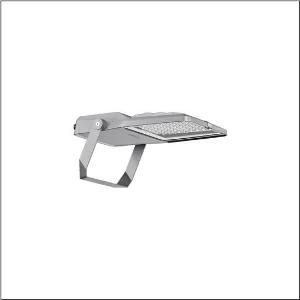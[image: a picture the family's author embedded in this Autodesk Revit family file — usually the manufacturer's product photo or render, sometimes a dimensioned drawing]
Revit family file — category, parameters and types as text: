
# Revit family: floodlight_fl_21_mini___pl61_5xa7776b2c1a_e1cc
name_source: partatom
category: Lighting Fixtures
units: mm (PartAtom-declared; Revit-internal decimal feet)

## family parameters
Cut with Voids When Loaded = No
Host = Face
Light Source = No
Part Type = Normal
Room Calculation Point = No
Round Connector Dimension = Use Diameter
Shared = No

## types (1)
- --- (1 x LED, 6110 lm, 45.7 W, 3000K)
    Apparent Load = 46 VA
    CIE Flux Codes = 33 65 98 100 100
    Color Rendering = 70
    Color Temperature = 3000K
    Default Elevation = 1800 mm
    Description = Floodlight FL 21 mini, floodlight, primary light control with lens, of PMMA, primary optical cover: protective disc, of toughened safety glass, transparent, light distribution: PL61, light emission: direct distribution, installation type: surface-mounted, LED, High Power LED, rated luminous flux: 6.110lm, luminous efficacy: 134lm/W, light colour: 730, colour temperature: 3000K, control: flexible luminous flux parameterisation, time-dependent luminous flux control, constant luminous flux control, overheat protection, presetting dimming logarithmic, with terminal, 6-pole, mains connection: 220..240V, AC, 50/60Hz, start of lifetime: 46W, end of service life: 48W, reduction: 22W, luminaire housing, of diecast aluminium, powder-coated, Siteco® metallic grey (DB 702S), corrosivity category C5 mid according to DIN EN ISO 12944, sealing non-destructively replaceable, mounting bracket, of steel, galvanised, powder-coated, Siteco® metallic grey (DB 702S), Smart Interface below and above, protection rating (complete): IP66, insulation class (complete): insulation class II (safety insulation), certification: CE, ENEC, VDE, protection symbol: D, impact resistance: IK08, permissible operating ambient temperature: -40..+40°C, permissible operating ambient temperature for outdoor applications: -40..+50°C, standard: DIN EN 12944, LABS conformity tested according to VDMA 24364:2018-05, packaging unit: 1 piece

Light Distribution: PL61
    Height = 70 mm
    Lamp = 1 x LED
    Lamp Light Flux = 6110 lm
    Lamp Power = 45.7 W
    Lamp count = 1
    Length = 485 mm
    Luminous efficacy = 134 lm/W
    Manufacturer = Siteco
    ModVariant = No
    Model = 5XA7776B2C1A
    Number of Poles = 1
    OnlyDefault = Yes
    Power Factor = 1
    Product Name = Floodlight FL 21 mini | PL61
    Product group = floodlight | pylon annexe
    ProductGroupID = 6200
    Protection Class = Protection class II
    Protection Degree = IP 66
    RLX_Detail_Level = 1
    RLX_Emergency_Light_Flux = 0 lm
    RLX_Emergency_Type = 0
    RLX_Emergency_Type_DB = No
    RlxData = <blob elided: 95921 chars, md5=8e675ca1>
    Socket = socket
    Standby Power = 0 W
    System Light Flux = 6110 lm
    System Power = 46 W
    Type Comments = factory setting: luminous flux: 100 % | dim-lin: 254 | 463 mA
    Type Image = l_1006845.jpg
    URL = http://relux.com
    VarID = @adj_105235
    Voltage = 0 V
    Weight = 0.00 kg
    Width = 337 mm

## geometry (parser evidence)
native form markers: Blend x4, Sweep x11
no freeform markers — native parametric forms only
